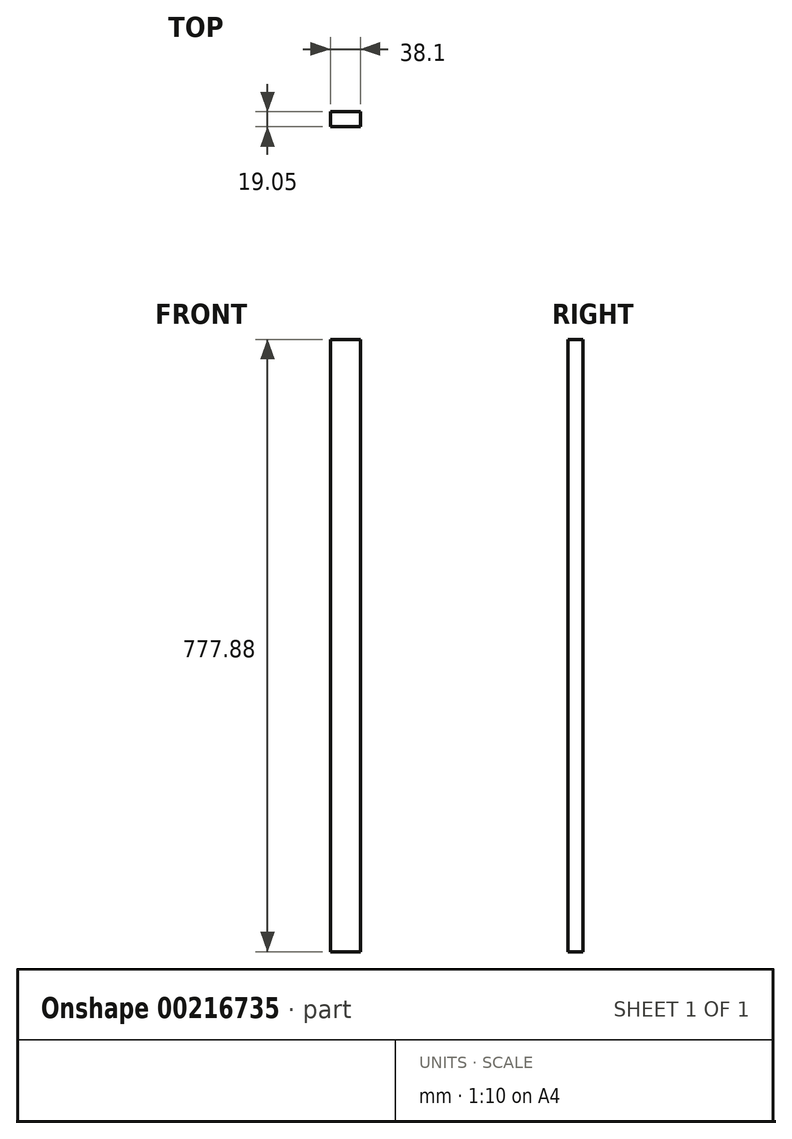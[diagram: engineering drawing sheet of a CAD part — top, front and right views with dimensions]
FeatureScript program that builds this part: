
annotation { "Feature Type Name" : "Feature", "Feature Type Description" : "" }
export const myFeature = defineFeature(function(context is Context, id is Id, definition is map)
    precondition{}
    {
        {
            var Q0;
            Q0=qCreatedBy(makeId("Front.planeOp"),FACE);
            var sketch = newSketch(context, id + "F0", { "sketchPlane" : qUnion([Q0])});
            skLineSegment(sketch, "E0.bottom", {"start": v(0, 0) * mm, "end": v(38.1, 0) * mm});
            skLineSegment(sketch, "E0.top", {"start": v(0, 777.88) * mm, "end": v(38.1, 777.88) * mm});
            skLineSegment(sketch, "E0.left", {"start": v(0, 0) * mm, "end": v(0, 777.88) * mm});
            skLineSegment(sketch, "E0.right", {"start": v(38.1, 0) * mm, "end": v(38.1, 777.88) * mm});
            skSolve(sketch);
        }
        {
            var Q0;
            Q0 = qSketchRegion(id + "F0", true);
            extrude(context, id + "F1", {"entities" : qUnion([Q0]), "depth" : 19.05 * mm});
        }
    });
